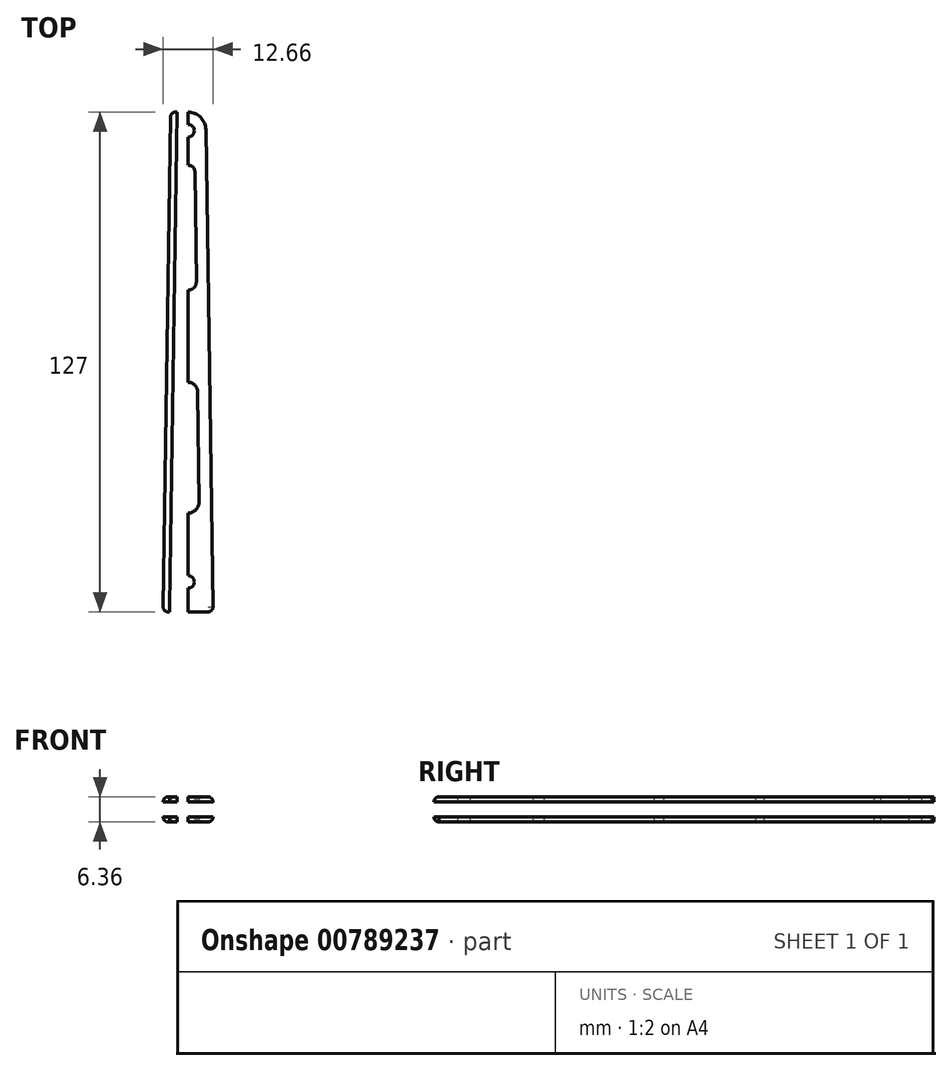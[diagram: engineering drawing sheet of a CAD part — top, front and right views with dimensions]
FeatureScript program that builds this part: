
annotation { "Feature Type Name" : "Feature", "Feature Type Description" : "" }
export const myFeature = defineFeature(function(context is Context, id is Id, definition is map)
    precondition{}
    {
        {
            var Q0;
            Q0=qCreatedBy(makeId("Top.planeOp"),FACE);
            var sketch = newSketch(context, id + "F0", { "sketchPlane" : qUnion([Q0])});
            skLineSegment(sketch, "E0", {"start": v(0, 0) * mm, "end": v(6.35, 0) * mm});
            skLineSegment(sketch, "E1", {"start": v(0, 0) * mm, "end": v(-6.35, 0) * mm});
            skLineSegment(sketch, "E2", {"start": v(0, 127) * mm, "end": v(-4.44, 127) * mm});
            skLineSegment(sketch, "E3", {"start": v(0, 127) * mm, "end": v(4.45, 127) * mm});
            skLineSegment(sketch, "E4", {"start": v(4.45, 127) * mm, "end": v(6.35, 0) * mm});
            skLineSegment(sketch, "E5", {"start": v(-4.44, 127) * mm, "end": v(-6.35, 0) * mm});
            skLineSegment(sketch, "E6", {"start": v(0, 127) * mm, "end": v(0, 0) * mm});
            skLineSegment(sketch, "E7", {"start": v(0, 127) * mm, "end": v(0, 123.83) * mm});
            skLineSegment(sketch, "E8", {"start": v(0, 123.83) * mm, "end": v(0, 122.24) * mm});
            skCircle(sketch, "E9", {"center": v(0, 122.24) * mm, "radius": 1.59 * mm});
            skLineSegment(sketch, "E10", {"start": v(0, 0) * mm, "end": v(0, 27.94) * mm});
            skLineSegment(sketch, "E11", {"start": v(0, 27.94) * mm, "end": v(0, 55.88) * mm});
            skLineSegment(sketch, "E12", {"start": v(0, 55.88) * mm, "end": v(0, 83.82) * mm});
            skLineSegment(sketch, "E13", {"start": v(0, 83.82) * mm, "end": v(0, 111.76) * mm});
            skArc(sketch, "E14", {"start": v(-1.72, 111.76) * mm, "mid": v(0, 113.48) * mm, "end": v(1.72, 111.76) * mm});
            skArc(sketch, "E15", {"start": v(2.09, 83.82) * mm, "mid": v(-0.03, 81.73) * mm, "end": v(-2.09, 83.87) * mm});
            skArc(sketch, "E16", {"start": v(2.45, 55.88) * mm, "mid": v(0.03, 58.33) * mm, "end": v(-2.45, 55.94) * mm});
            skArc(sketch, "E17", {"start": v(2.81, 27.94) * mm, "mid": v(-0.04, 25.13) * mm, "end": v(-2.81, 28.01) * mm});
            skLineSegment(sketch, "E18", {"start": v(0, 0) * mm, "end": v(0, 7.62) * mm});
            skCircle(sketch, "E19", {"center": v(0, 7.62) * mm, "radius": 1.59 * mm});
            skLineSegment(sketch, "E20", {"start": v(-3.18, 0) * mm, "end": v(-6.35, 0) * mm});
            skLineSegment(sketch, "E21", {"start": v(-4.76, 0) * mm, "end": v(-2.86, 127) * mm});
            skLineSegment(sketch, "E22", {"start": v(0, 7.62) * mm, "end": v(0, 15.24) * mm});
            skLineSegment(sketch, "E23", {"start": v(0, 122.24) * mm, "end": v(0, 117.54) * mm});
            skLineSegment(sketch, "E24", {"start": v(-1.72, 111.76) * mm, "end": v(-2.09, 83.87) * mm});
            skLineSegment(sketch, "E25", {"start": v(-2.45, 55.94) * mm, "end": v(-2.81, 28.01) * mm});
            skLineSegment(sketch, "E26", {"start": v(2.45, 55.88) * mm, "end": v(2.81, 27.94) * mm});
            skLineSegment(sketch, "E27", {"start": v(1.72, 111.76) * mm, "end": v(2.09, 83.82) * mm});
            skLineSegment(sketch, "E28", {"start": v(-3.06, 113.48) * mm, "end": v(-4.65, 113.48) * mm});
            skPoint(sketch, "E28.startSnap0", {"position": v(0, 113.48) * mm});
            skSolve(sketch);
        }
        {
            var Q0;
            {var subQ20=sQuery(id+"F0.wireOp",EDGE,"E0");Q0=makeQuery(id+"F0.imprint","IMPRINT",FACE,{"disambiguationData":[TD([[makeQuery(id+"F0.imprint","IMPRINT",EDGE,{"derivedFrom":subQ20}),1.0]])]});}
            var Q1;
            {var subQ13=sQuery(id+"F0.wireOp",EDGE,"E1");Q1=makeQuery(id+"F0.imprint","IMPRINT",FACE,{"disambiguationData":[TD([[makeQuery(id+"F0.imprint","IMPRINT",EDGE,{"derivedFrom":subQ13}),-1.0]])]});}
            var Q2;
            {var subQ0=sQuery(id+"F0.wireOp",EDGE,"E5");Q2=makeQuery(id+"F0.imprint","IMPRINT",FACE,{"disambiguationData":[TD([[makeQuery(id+"F0.imprint","IMPRINT",EDGE,{"derivedFrom":subQ0}),1.0]])]});}
            extrude(context, id + "F1", {"entities" : qUnion([Q0, Q1, Q2]), "endBound" : BoundingType.SYMMETRIC, "depth" : 6.35 * mm, "offsetDistance" : 25.4 * mm});
        }
        {
            var Q0;
            {var subQ20=sQuery(id+"F0.wireOp",EDGE,"E0");Q0=makeQuery(id+"F0.imprint","IMPRINT",FACE,{"disambiguationData":[TD([[makeQuery(id+"F0.imprint","IMPRINT",EDGE,{"derivedFrom":subQ20}),1.0]])]});}
            var Q1;
            {var subQ13=sQuery(id+"F0.wireOp",EDGE,"E1");Q1=makeQuery(id+"F0.imprint","IMPRINT",FACE,{"disambiguationData":[TD([[makeQuery(id+"F0.imprint","IMPRINT",EDGE,{"derivedFrom":subQ13}),-1.0]])]});}
            var Q2;
            {var subQ5=sQuery(id+"F0.wireOp",EDGE,"E28");Q2=makeQuery(id+"F0.imprint","IMPRINT",FACE,{"disambiguationData":[TD([[makeQuery(id+"F0.imprint","IMPRINT",EDGE,{"derivedFrom":subQ5}),-1.0]])]});}
            extrude(context, id + "F2", {"entities" : qUnion([Q0, Q1, Q2]), "operationType" : NewBodyOperationType.REMOVE, "endBound" : BoundingType.SYMMETRIC, "oppositeDirection" : true, "depth" : 3.8 * mm, "offsetDistance" : 25.4 * mm});
        }
        {
            var Q0;
            {var subQ0=sQuery(id+"F0.wireOp",EDGE,"E27");var subQ1=sQuery(id+"F0.wireOp",EDGE,"E26");var subQ2=sQuery(id+"F0.wireOp",EDGE,"E25");var subQ3=sQuery(id+"F0.wireOp",EDGE,"E24");var subQ4=sQuery(id+"F0.wireOp",EDGE,"E20");var subQ5=sQuery(id+"F0.wireOp",EDGE,"E19");var subQ6=sQuery(id+"F0.wireOp",EDGE,"E17");var subQ7=sQuery(id+"F0.wireOp",EDGE,"E16");var subQ8=sQuery(id+"F0.wireOp",EDGE,"E15");var subQ9=sQuery(id+"F0.wireOp",EDGE,"E14");var subQ10=sQuery(id+"F0.wireOp",EDGE,"E9");var subQ11=sQuery(id+"F0.wireOp",EDGE,"E5");var subQ12=sQuery(id+"F0.wireOp",EDGE,"E4");var subQ13=sQuery(id+"F0.wireOp",EDGE,"E3");var subQ14=sQuery(id+"F0.wireOp",EDGE,"E2");var subQ15=sQuery(id+"F0.wireOp",EDGE,"E1");var subQ16=sQuery(id+"F0.wireOp",EDGE,"E0");Q0=makeQuery(id+"F2.boolean.opBoolean","SPLIT",EDGE,{"disambiguationData":[TD([makeQuery(id+"F1.opExtrude","CAP_FACE",FACE,{"disambiguationData":[OSD([subQ16,subQ15,subQ14,subQ13,subQ12,subQ11,subQ10,subQ9,subQ8,subQ7,subQ6,subQ5,subQ4,subQ3,subQ2,subQ1,subQ0])],"isStart":true})])],"derivedFrom":makeQuery(id+"F1.opExtrude","SWEPT_EDGE",EDGE,{"disambiguationData":[OSD([subQ14,subQ11])]})});}
            var Q1;
            {var subQ0=sQuery(id+"F0.wireOp",EDGE,"E27");var subQ1=sQuery(id+"F0.wireOp",EDGE,"E26");var subQ2=sQuery(id+"F0.wireOp",EDGE,"E25");var subQ3=sQuery(id+"F0.wireOp",EDGE,"E24");var subQ4=sQuery(id+"F0.wireOp",EDGE,"E20");var subQ5=sQuery(id+"F0.wireOp",EDGE,"E19");var subQ6=sQuery(id+"F0.wireOp",EDGE,"E17");var subQ7=sQuery(id+"F0.wireOp",EDGE,"E16");var subQ8=sQuery(id+"F0.wireOp",EDGE,"E15");var subQ9=sQuery(id+"F0.wireOp",EDGE,"E14");var subQ10=sQuery(id+"F0.wireOp",EDGE,"E9");var subQ11=sQuery(id+"F0.wireOp",EDGE,"E5");var subQ12=sQuery(id+"F0.wireOp",EDGE,"E4");var subQ13=sQuery(id+"F0.wireOp",EDGE,"E3");var subQ14=sQuery(id+"F0.wireOp",EDGE,"E2");var subQ15=sQuery(id+"F0.wireOp",EDGE,"E1");var subQ16=sQuery(id+"F0.wireOp",EDGE,"E0");Q1=makeQuery(id+"F2.boolean.opBoolean","SPLIT",EDGE,{"disambiguationData":[TD([makeQuery(id+"F1.opExtrude","CAP_FACE",FACE,{"disambiguationData":[OSD([subQ16,subQ15,subQ14,subQ13,subQ12,subQ11,subQ10,subQ9,subQ8,subQ7,subQ6,subQ5,subQ4,subQ3,subQ2,subQ1,subQ0])],"isStart":false})])],"derivedFrom":makeQuery(id+"F1.opExtrude","SWEPT_EDGE",EDGE,{"disambiguationData":[OSD([subQ14,subQ11])]})});}
            var Q2;
            {var subQ0=sQuery(id+"F0.wireOp",EDGE,"E27");var subQ1=sQuery(id+"F0.wireOp",EDGE,"E26");var subQ2=sQuery(id+"F0.wireOp",EDGE,"E25");var subQ3=sQuery(id+"F0.wireOp",EDGE,"E24");var subQ4=sQuery(id+"F0.wireOp",EDGE,"E20");var subQ5=sQuery(id+"F0.wireOp",EDGE,"E19");var subQ6=sQuery(id+"F0.wireOp",EDGE,"E17");var subQ7=sQuery(id+"F0.wireOp",EDGE,"E16");var subQ8=sQuery(id+"F0.wireOp",EDGE,"E15");var subQ9=sQuery(id+"F0.wireOp",EDGE,"E14");var subQ10=sQuery(id+"F0.wireOp",EDGE,"E9");var subQ11=sQuery(id+"F0.wireOp",EDGE,"E5");var subQ12=sQuery(id+"F0.wireOp",EDGE,"E4");var subQ13=sQuery(id+"F0.wireOp",EDGE,"E3");var subQ14=sQuery(id+"F0.wireOp",EDGE,"E2");var subQ15=sQuery(id+"F0.wireOp",EDGE,"E1");var subQ16=sQuery(id+"F0.wireOp",EDGE,"E0");Q2=makeQuery(id+"F2.boolean.opBoolean","SPLIT",EDGE,{"disambiguationData":[TD([makeQuery(id+"F1.opExtrude","CAP_FACE",FACE,{"disambiguationData":[OSD([subQ16,subQ15,subQ14,subQ13,subQ12,subQ11,subQ10,subQ9,subQ8,subQ7,subQ6,subQ5,subQ4,subQ3,subQ2,subQ1,subQ0])],"isStart":false})])],"derivedFrom":makeQuery(id+"F1.opExtrude","SWEPT_EDGE",EDGE,{"disambiguationData":[OSD([subQ13,subQ12])]})});}
            var Q3;
            {var subQ0=sQuery(id+"F0.wireOp",EDGE,"E27");var subQ1=sQuery(id+"F0.wireOp",EDGE,"E26");var subQ2=sQuery(id+"F0.wireOp",EDGE,"E25");var subQ3=sQuery(id+"F0.wireOp",EDGE,"E24");var subQ4=sQuery(id+"F0.wireOp",EDGE,"E20");var subQ5=sQuery(id+"F0.wireOp",EDGE,"E19");var subQ6=sQuery(id+"F0.wireOp",EDGE,"E17");var subQ7=sQuery(id+"F0.wireOp",EDGE,"E16");var subQ8=sQuery(id+"F0.wireOp",EDGE,"E15");var subQ9=sQuery(id+"F0.wireOp",EDGE,"E14");var subQ10=sQuery(id+"F0.wireOp",EDGE,"E9");var subQ11=sQuery(id+"F0.wireOp",EDGE,"E5");var subQ12=sQuery(id+"F0.wireOp",EDGE,"E4");var subQ13=sQuery(id+"F0.wireOp",EDGE,"E3");var subQ14=sQuery(id+"F0.wireOp",EDGE,"E2");var subQ15=sQuery(id+"F0.wireOp",EDGE,"E1");var subQ16=sQuery(id+"F0.wireOp",EDGE,"E0");Q3=makeQuery(id+"F2.boolean.opBoolean","SPLIT",EDGE,{"disambiguationData":[TD([makeQuery(id+"F1.opExtrude","CAP_FACE",FACE,{"disambiguationData":[OSD([subQ16,subQ15,subQ14,subQ13,subQ12,subQ11,subQ10,subQ9,subQ8,subQ7,subQ6,subQ5,subQ4,subQ3,subQ2,subQ1,subQ0])],"isStart":true})])],"derivedFrom":makeQuery(id+"F1.opExtrude","SWEPT_EDGE",EDGE,{"disambiguationData":[OSD([subQ13,subQ12])]})});}
            fillet(context, id + "F3", {"entities" : qUnion([Q0, Q1, Q2, Q3]), "radius" : 4.57 * mm, "tangentPropagation" : true, "allowEdgeOverflow" : false});
        }
        {
            var Q0;
            Q0=makeQuery(id+"F1.opExtrude","CAP_EDGE",EDGE,{"disambiguationData":[OSD([sQuery(id+"F0.wireOp",EDGE,"E4")])],"isStart":true});
            var Q1;
            Q1=makeQuery(id+"F1.opExtrude","SWEPT_EDGE",EDGE,{"disambiguationData":[OSD([sQuery(id+"F0.wireOp",EDGE,"E5"),sQuery(id+"F0.wireOp",EDGE,"E20")])]});
            var Q2;
            {var subQ0=sQuery(id+"F0.wireOp",EDGE,"E27");var subQ1=sQuery(id+"F0.wireOp",EDGE,"E26");var subQ2=sQuery(id+"F0.wireOp",EDGE,"E25");var subQ3=sQuery(id+"F0.wireOp",EDGE,"E24");var subQ4=sQuery(id+"F0.wireOp",EDGE,"E20");var subQ5=sQuery(id+"F0.wireOp",EDGE,"E19");var subQ6=sQuery(id+"F0.wireOp",EDGE,"E17");var subQ7=sQuery(id+"F0.wireOp",EDGE,"E16");var subQ8=sQuery(id+"F0.wireOp",EDGE,"E15");var subQ9=sQuery(id+"F0.wireOp",EDGE,"E14");var subQ10=sQuery(id+"F0.wireOp",EDGE,"E9");var subQ11=sQuery(id+"F0.wireOp",EDGE,"E5");var subQ12=sQuery(id+"F0.wireOp",EDGE,"E4");var subQ13=sQuery(id+"F0.wireOp",EDGE,"E3");var subQ14=sQuery(id+"F0.wireOp",EDGE,"E2");var subQ15=sQuery(id+"F0.wireOp",EDGE,"E1");var subQ16=sQuery(id+"F0.wireOp",EDGE,"E0");Q2=makeQuery(id+"F2.boolean.opBoolean","SPLIT",EDGE,{"disambiguationData":[TD([makeQuery(id+"F1.opExtrude","CAP_FACE",FACE,{"disambiguationData":[OSD([subQ16,subQ15,subQ14,subQ13,subQ12,subQ11,subQ10,subQ9,subQ8,subQ7,subQ6,subQ5,subQ4,subQ3,subQ2,subQ1,subQ0])],"isStart":false})])],"derivedFrom":makeQuery(id+"F1.opExtrude","SWEPT_EDGE",EDGE,{"disambiguationData":[OSD([subQ16,subQ12])]})});}
            var Q3;
            {var subQ0=sQuery(id+"F0.wireOp",EDGE,"E27");var subQ1=sQuery(id+"F0.wireOp",EDGE,"E26");var subQ2=sQuery(id+"F0.wireOp",EDGE,"E25");var subQ3=sQuery(id+"F0.wireOp",EDGE,"E24");var subQ4=sQuery(id+"F0.wireOp",EDGE,"E20");var subQ5=sQuery(id+"F0.wireOp",EDGE,"E19");var subQ6=sQuery(id+"F0.wireOp",EDGE,"E17");var subQ7=sQuery(id+"F0.wireOp",EDGE,"E16");var subQ8=sQuery(id+"F0.wireOp",EDGE,"E15");var subQ9=sQuery(id+"F0.wireOp",EDGE,"E14");var subQ10=sQuery(id+"F0.wireOp",EDGE,"E9");var subQ11=sQuery(id+"F0.wireOp",EDGE,"E5");var subQ12=sQuery(id+"F0.wireOp",EDGE,"E4");var subQ13=sQuery(id+"F0.wireOp",EDGE,"E3");var subQ14=sQuery(id+"F0.wireOp",EDGE,"E2");var subQ15=sQuery(id+"F0.wireOp",EDGE,"E1");var subQ16=sQuery(id+"F0.wireOp",EDGE,"E0");Q3=makeQuery(id+"F2.boolean.opBoolean","SPLIT",EDGE,{"disambiguationData":[TD([makeQuery(id+"F1.opExtrude","CAP_FACE",FACE,{"disambiguationData":[OSD([subQ16,subQ15,subQ14,subQ13,subQ12,subQ11,subQ10,subQ9,subQ8,subQ7,subQ6,subQ5,subQ4,subQ3,subQ2,subQ1,subQ0])],"isStart":true})])],"derivedFrom":makeQuery(id+"F1.opExtrude","SWEPT_EDGE",EDGE,{"disambiguationData":[OSD([subQ16,subQ12])]})});}
            var Q4;
            Q4=makeQuery(id+"F1.opExtrude","CAP_EDGE",EDGE,{"disambiguationData":[OSD([sQuery(id+"F0.wireOp",EDGE,"E5")])],"isStart":false});
            var Q5;
            Q5=makeQuery(id+"F1.opExtrude","CAP_EDGE",EDGE,{"disambiguationData":[OSD([sQuery(id+"F0.wireOp",EDGE,"E5")])],"isStart":true});
            var Q6;
            Q6=makeQuery(id+"F1.opExtrude","CAP_EDGE",EDGE,{"disambiguationData":[OSD([sQuery(id+"F0.wireOp",EDGE,"E4")])],"isStart":false});
            var Q7;
            Q7=makeQuery(id+"F1.opExtrude","CAP_EDGE",EDGE,{"disambiguationData":[OSD([sQuery(id+"F0.wireOp",EDGE,"E0"),sQuery(id+"F0.wireOp",EDGE,"E1"),sQuery(id+"F0.wireOp",EDGE,"E20")])],"isStart":true});
            var Q8;
            Q8=makeQuery(id+"F1.opExtrude","CAP_EDGE",EDGE,{"disambiguationData":[OSD([sQuery(id+"F0.wireOp",EDGE,"E0"),sQuery(id+"F0.wireOp",EDGE,"E1"),sQuery(id+"F0.wireOp",EDGE,"E20")])],"isStart":false});
            fillet(context, id + "F4", {"entities" : qUnion([Q0, Q1, Q2, Q3, Q4, Q5, Q6, Q7, Q8]), "radius" : 1.27 * mm, "tangentPropagation" : true, "allowEdgeOverflow" : false});
        }
    });
